# Revit family: Haworth_Immerse_ShiftTable_RectangularRectangular_EU_PRELIMINARY
name_source: partatom
category: Furniture Systems
revit_build: Autodesk Revit 2018 (Build: 20170223_1515(x64)
units: mm (PartAtom-declared; Revit-internal decimal feet)

## family parameters
Always vertical = Yes
Cut with Voids When Loaded = No
OmniClass Number = 23.40.70.14.64.21
OmniClass Title = Systems Furniture
Part Type = Normal
Room Calculation Point = No
Round Connector Dimension = Use Diameter
Shared = No
Work Plane-Based = No

## types (3) — shared parameters
Actual Depth = 150 cm
Actual Height = 74 cm
Actual Width = 400 cm
Assembly Code = E2020200
Cable Finish = Haworth _ Polymer _ Undecided
Cable Height = 9 cm
Description = Haworth - Immerse - Shift Table - Rectangular / Rectangular
Manufacturer = Haworth
Model = IMSHRR4427
Revision Number = 1
Size = Verify Final Dim. w/ Haworth
Snake Cable Lower = Yes
Snake Cable Upper = Yes
URL = https://www.haworth.com
URL - Product = https://www.haworth.com
Void Baseline Height = 46 cm
Warranty = http://www.haworth.com

## per-type parameters (varying)
| type | Oblong Planter | Oblong Planter Void Height | Round Planter | Round Planter Void Height |
| 200w 150d 240w 120d 74h - with two Planters | Yes | 56 cm | Yes | 61 cm |
| 200w 150d 240w 120d 74h - with Round Planter | No | 15 cm | Yes | 61 cm |
| 200w 150d 240w 120d 74h - with Oblong Planter | Yes | 56 cm | No | 15 cm |

## geometry (parser evidence)
native form markers: Sweep x7
no freeform markers — native parametric forms only
